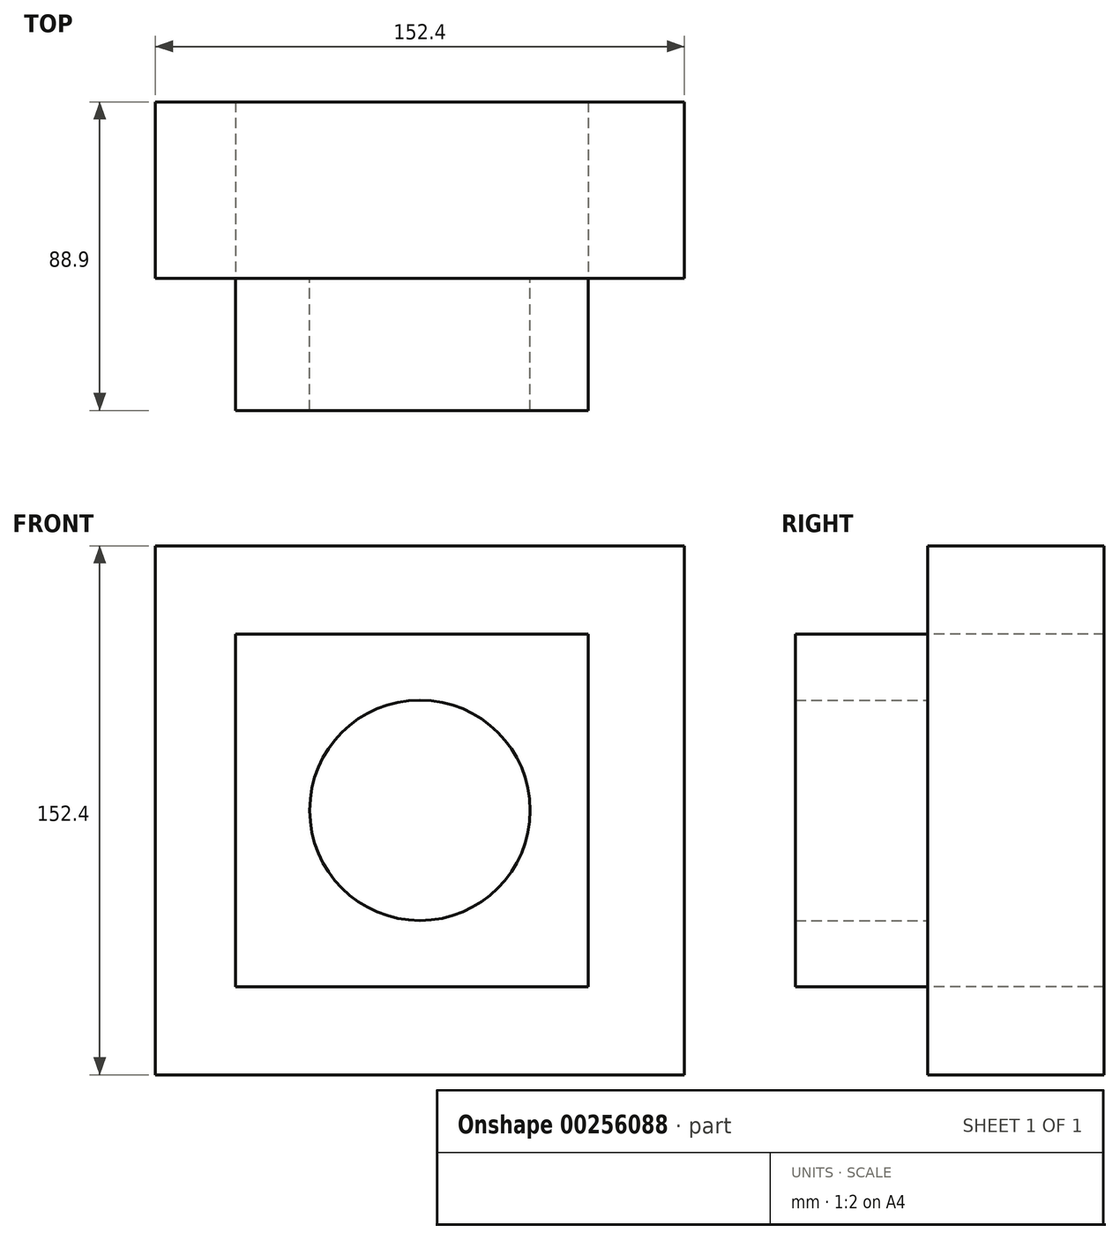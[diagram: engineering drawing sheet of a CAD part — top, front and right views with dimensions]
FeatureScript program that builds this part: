
annotation { "Feature Type Name" : "Feature", "Feature Type Description" : "" }
export const myFeature = defineFeature(function(context is Context, id is Id, definition is map)
    precondition{}
    {
        {
            var Q0;
            Q0=qCreatedBy(makeId("Front.planeOp"),FACE);
            var sketch = newSketch(context, id + "F0", { "sketchPlane" : qUnion([Q0])});
            skCircle(sketch, "E0", {"center": v(0, 0) * mm, "radius": 31.75 * mm});
            skLineSegment(sketch, "E1.bottom", {"start": v(-53.16, 50.8) * mm, "end": v(48.44, 50.8) * mm});
            skLineSegment(sketch, "E1.top", {"start": v(-53.16, -50.8) * mm, "end": v(48.44, -50.8) * mm});
            skLineSegment(sketch, "E1.left", {"start": v(-53.16, 50.8) * mm, "end": v(-53.16, -50.8) * mm});
            skLineSegment(sketch, "E1.right", {"start": v(48.44, 50.8) * mm, "end": v(48.44, -50.8) * mm});
            skPoint(sketch, "E1.middle", {"position": v(-2.36, 0) * mm});
            skLineSegment(sketch, "E2.bottom", {"start": v(-76.2, 76.2) * mm, "end": v(76.2, 76.2) * mm});
            skLineSegment(sketch, "E2.top", {"start": v(-76.2, -76.2) * mm, "end": v(76.2, -76.2) * mm});
            skLineSegment(sketch, "E2.left", {"start": v(-76.2, 76.2) * mm, "end": v(-76.2, -76.2) * mm});
            skLineSegment(sketch, "E2.right", {"start": v(76.2, 76.2) * mm, "end": v(76.2, -76.2) * mm});
            skSolve(sketch);
        }
        {
            var Q0;
            Q0=makeQuery(id+"F0.imprint","IMPRINT",FACE,{"disambiguationData":[TD([[makeQuery(id+"F0.imprint","IMPRINT",EDGE,{"derivedFrom":sQuery(id+"F0.wireOp",EDGE,"E0")}),-1.0]])]});
            extrude(context, id + "F1", {"entities" : qUnion([Q0]), "depth" : 38.1 * mm});
        }
        {
            var Q0;
            Q0=makeQuery(id+"F0.imprint","IMPRINT",FACE,{"disambiguationData":[TD([[makeQuery(id+"F0.imprint","IMPRINT",EDGE,{"derivedFrom":sQuery(id+"F0.wireOp",EDGE,"E1.bottom")}),1.0]])]});
            extrude(context, id + "F2", {"entities" : qUnion([Q0]), "operationType" : NewBodyOperationType.ADD, "oppositeDirection" : true, "depth" : 50.8 * mm});
        }
    });
